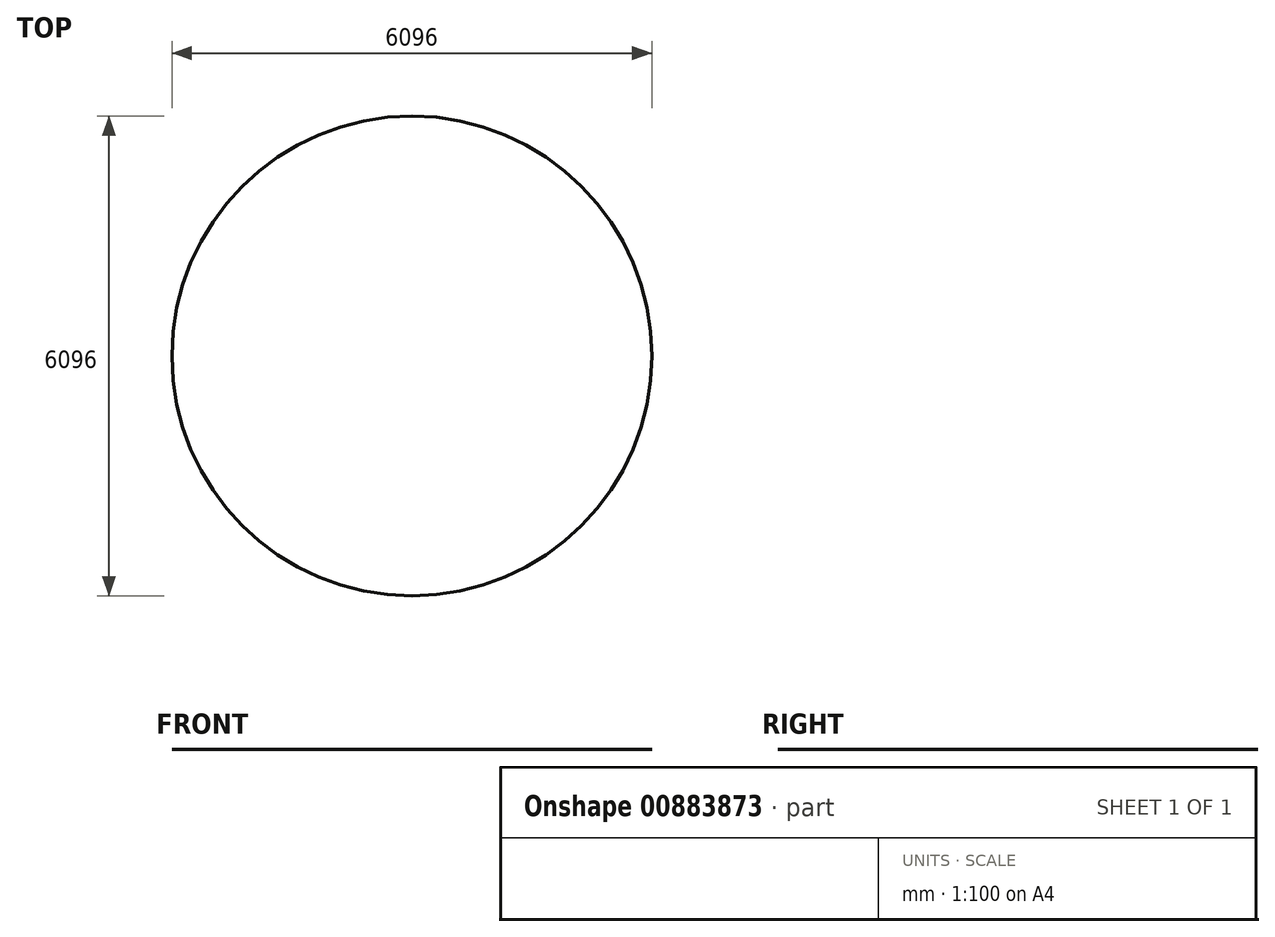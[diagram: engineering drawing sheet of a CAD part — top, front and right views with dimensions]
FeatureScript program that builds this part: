
annotation { "Feature Type Name" : "Feature", "Feature Type Description" : "" }
export const myFeature = defineFeature(function(context is Context, id is Id, definition is map)
    precondition{}
    {
        {
            var Q0;
            Q0=qCreatedBy(makeId("Top.planeOp"),FACE);
            var sketch = newSketch(context, id + "F0", { "sketchPlane" : qUnion([Q0])});
            skCircle(sketch, "E0", {"center": v(0, 0) * mm, "radius": 3048 * mm});
            skSolve(sketch);
        }
        {
            var Q0;
            Q0=makeQuery(id+"F0.imprint","IMPRINT",FACE,{"disambiguationData":[TD([[makeQuery(id+"F0.imprint","IMPRINT",EDGE,{"derivedFrom":sQuery(id+"F0.wireOp",EDGE,"E0")}),1.0]])]});
            extrude(context, id + "F1", {"entities" : qUnion([Q0]), "depth" : 1 / 203.2 * mm, "offsetDistance" : 25.4 * mm});
        }
    });
